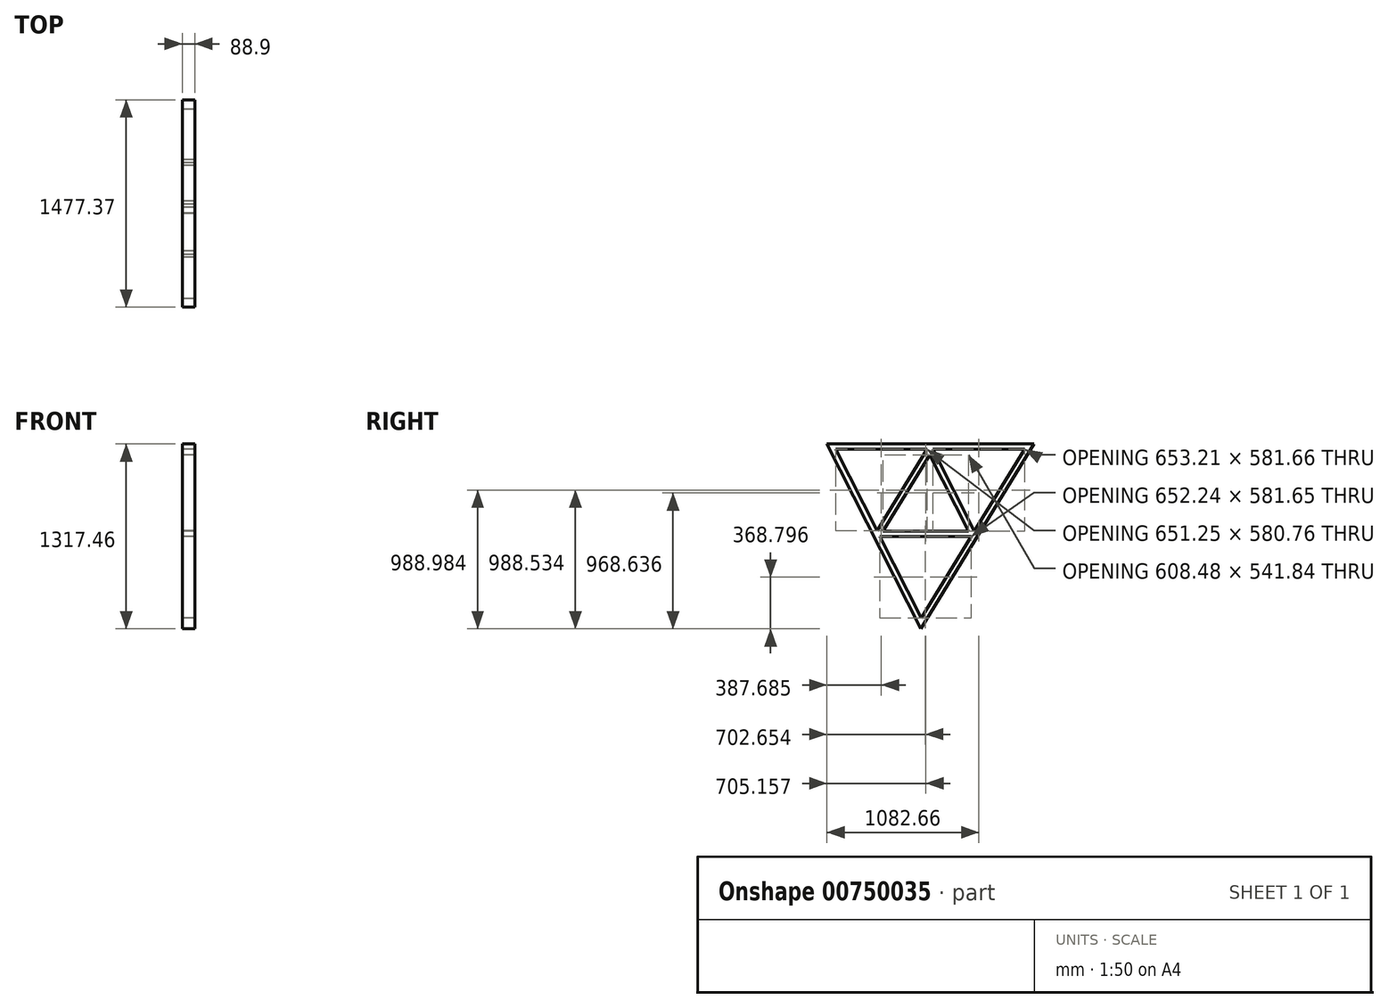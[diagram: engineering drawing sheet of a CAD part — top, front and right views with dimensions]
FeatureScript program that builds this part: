
annotation { "Feature Type Name" : "Feature", "Feature Type Description" : "" }
export const myFeature = defineFeature(function(context is Context, id is Id, definition is map)
    precondition{}
    {
        {
            var Q0;
            Q0=qCreatedBy(makeId("Right.planeOp"),FACE);
            var sketch = newSketch(context, id + "F0", { "sketchPlane" : qUnion([Q0])});
            skLineSegment(sketch, "E0", {"start": v(-713.3, 448.31) * mm, "end": v(764.06, 448.31) * mm});
            skLineSegment(sketch, "E1", {"start": v(764.06, 448.31) * mm, "end": v(-44.8, -869.15) * mm});
            skLineSegment(sketch, "E2", {"start": v(-44.8, -869.15) * mm, "end": v(-713.3, 448.31) * mm});
            skLineSegment(sketch, "E3", {"start": v(-41.64, -791.18) * mm, "end": v(695.96, 410.21) * mm});
            skLineSegment(sketch, "E4", {"start": v(695.96, 410.21) * mm, "end": v(-651.25, 410.21) * mm});
            skLineSegment(sketch, "E5", {"start": v(-651.25, 410.21) * mm, "end": v(-41.64, -791.18) * mm});
            skLineSegment(sketch, "E6", {"start": v(338.85, -171.45) * mm, "end": v(42.75, 410.21) * mm});
            skLineSegment(sketch, "E7", {"start": v(42.75, 410.21) * mm, "end": v(0, 410.21) * mm});
            skLineSegment(sketch, "E8", {"start": v(0, 410.21) * mm, "end": v(-356.56, -170.55) * mm});
            skLineSegment(sketch, "E9", {"start": v(-356.56, -170.55) * mm, "end": v(-336.78, -209.53) * mm});
            skLineSegment(sketch, "E10", {"start": v(-336.78, -209.53) * mm, "end": v(315.47, -209.53) * mm});
            skLineSegment(sketch, "E11", {"start": v(296.09, -171.43) * mm, "end": v(0, 410.21) * mm});
            skLineSegment(sketch, "E12", {"start": v(20.27, 370.4) * mm, "end": v(-336.33, -210.42) * mm});
            skLineSegment(sketch, "E13", {"start": v(-312.4, -171.43) * mm, "end": v(338.86, -171.43) * mm});
            skSolve(sketch);
        }
        {
            var Q0;
            Q0=makeQuery(id+"F0.imprint","IMPRINT",FACE,{"disambiguationData":[TD([[makeQuery(id+"F0.imprint","IMPRINT",EDGE,{"derivedFrom":sQuery(id+"F0.wireOp",EDGE,"E0")}),-1.0]])]});
            var Q1;
            {var subQ1=sQuery(id+"F0.wireOp",EDGE,"E8");Q1=makeQuery(id+"F0.imprint","IMPRINT",FACE,{"disambiguationData":[TD([[makeQuery(id+"F0.imprint","IMPRINT",EDGE,{"derivedFrom":subQ1}),1.0]])]});}
            var Q2;
            {var subQ4=sQuery(id+"F0.wireOp",EDGE,"E6");var subQ6=sQuery(id+"F0.wireOp",EDGE,"E13");var subQ8=makeQuery(id+"F0.imprint","INTERSECT",VERTEX,{"derivedFrom":[subQ4,subQ6]});Q2=makeQuery(id+"F0.imprint","IMPRINT",FACE,{"disambiguationData":[TD([[makeQuery(id+"F0.imprint","IMPRINT",EDGE,{"disambiguationData":[TD([[subQ8,-1.0]])],"derivedFrom":subQ4}),1.0]])]});}
            var Q3;
            {var subQ1=sQuery(id+"F0.wireOp",EDGE,"E10");var subQ5=sQuery(id+"F0.wireOp",EDGE,"E3");var subQ6=makeQuery(id+"F0.imprint","INTERSECT",VERTEX,{"derivedFrom":[subQ5,subQ1]});Q3=makeQuery(id+"F0.imprint","IMPRINT",FACE,{"disambiguationData":[TD([[makeQuery(id+"F0.imprint","IMPRINT",EDGE,{"disambiguationData":[TD([[subQ6,-1.0]])],"derivedFrom":subQ5}),1.0]])]});}
            extrude(context, id + "F1", {"entities" : qUnion([Q0, Q1, Q2, Q3]), "endBound" : BoundingType.SYMMETRIC, "depth" : 88.9 * mm, "offsetDistance" : 25.4 * mm});
        }
    });
